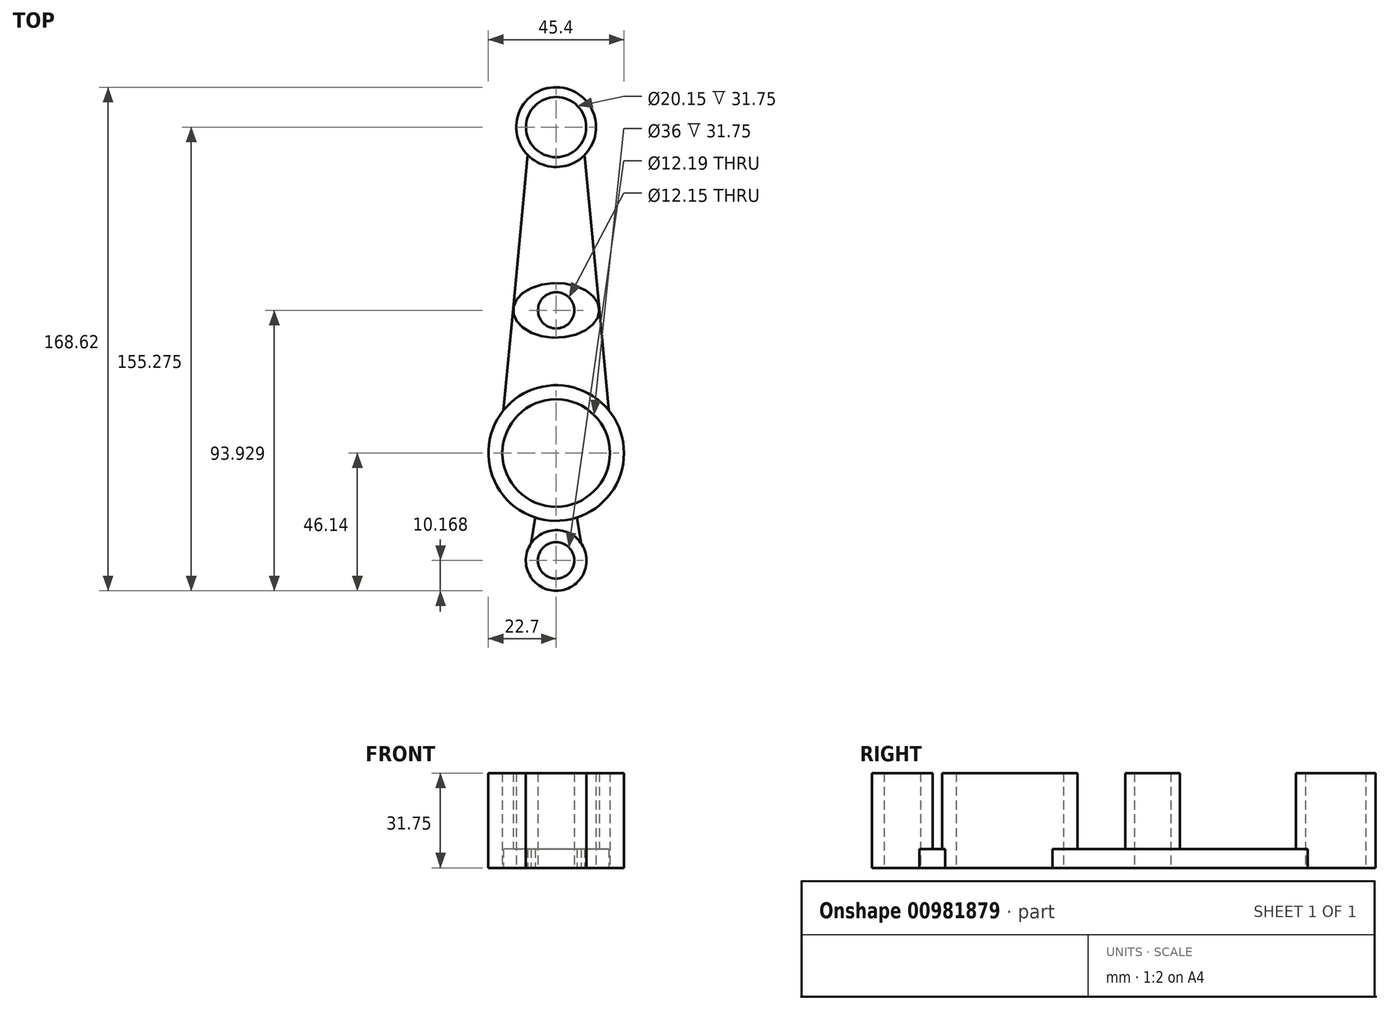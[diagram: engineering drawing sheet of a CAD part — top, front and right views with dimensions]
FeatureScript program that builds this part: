
annotation { "Feature Type Name" : "Feature", "Feature Type Description" : "" }
export const myFeature = defineFeature(function(context is Context, id is Id, definition is map)
    precondition{}
    {
        {
            var Q0;
            Q0=qCreatedBy(makeId("Top.planeOp"),FACE);
            var sketch = newSketch(context, id + "F0", { "sketchPlane" : qUnion([Q0])});
            skCircle(sketch, "E0", {"center": v(0, 0) * mm, "radius": 18 * mm});
            skCircle(sketch, "E1", {"center": v(0, 0) * mm, "radius": 22.7 * mm});
            skCircle(sketch, "E2", {"center": v(0, -35.97) * mm, "radius": 6.1 * mm});
            skCircle(sketch, "E3", {"center": v(0, -35.97) * mm, "radius": 10.16 * mm});
            skCircle(sketch, "E4", {"center": v(0, 47.79) * mm, "radius": 6.07 * mm});
            skCircle(sketch, "E5", {"center": v(0, 109.13) * mm, "radius": 10.08 * mm});
            skCircle(sketch, "E6", {"center": v(0, 109.13) * mm, "radius": 13.35 * mm});
            skEllipse(sketch, "E7", {"center": v(0, 47.79) * mm, "majorRadius": 14.42 * mm, "minorRadius": 9.82 * mm, "majorAxis": v(1, 0)});
            skLineSegment(sketch, "E8", {"start": v(0, 109.13) * mm, "end": v(0, 0) * mm, "construction": true});
            skPoint(sketch, "E9.endSnap0", {"position": v(14.42, 47.79) * mm});
            skLineSegment(sketch, "E10", {"start": v(9.52, 99.78) * mm, "end": v(17.63, 14.3) * mm});
            skLineSegment(sketch, "E11.MirrorCS", {"start": v(-9.52, 99.78) * mm, "end": v(-17.63, 14.3) * mm});
            skLineSegment(sketch, "E12", {"start": v(7.02, -21.58) * mm, "end": v(8.42, -30.27) * mm});
            skLineSegment(sketch, "E13.MirrorCS", {"start": v(-7.02, -21.58) * mm, "end": v(-8.42, -30.27) * mm});
            skSolve(sketch);
        }
        {
            var Q0;
            Q0 = qSketchRegion(id + "F0", true);
            extrude(context, id + "F1", {"entities" : qUnion([Q0]), "depth" : 6.35 * mm, "offsetDistance" : 25.4 * mm});
        }
        {
            var Q0;
            Q0=makeQuery(id+"F1.opExtrude","CAP_FACE",FACE,{"disambiguationData":[OSD([sQuery(id+"F0.wireOp",EDGE,"E0"),sQuery(id+"F0.wireOp",EDGE,"E1"),sQuery(id+"F0.wireOp",EDGE,"E2"),sQuery(id+"F0.wireOp",EDGE,"E3"),sQuery(id+"F0.wireOp",EDGE,"E4"),sQuery(id+"F0.wireOp",EDGE,"E5"),sQuery(id+"F0.wireOp",EDGE,"E6"),sQuery(id+"F0.wireOp",EDGE,"E10"),sQuery(id+"F0.wireOp",EDGE,"E11.MirrorCS"),sQuery(id+"F0.wireOp",EDGE,"E12"),sQuery(id+"F0.wireOp",EDGE,"E13.MirrorCS")])],"isStart":false});
            var sketch = newSketch(context, id + "F2", { "sketchPlane" : qUnion([Q0])});
            skCircle(sketch, "E14", {"center": v(0, 0) * mm, "radius": 18 * mm});
            skCircle(sketch, "E15", {"center": v(0, 0) * mm, "radius": 22.7 * mm});
            skCircle(sketch, "E16", {"center": v(0, -35.97) * mm, "radius": 6.1 * mm});
            skCircle(sketch, "E17", {"center": v(0, -35.97) * mm, "radius": 10.16 * mm});
            skCircle(sketch, "E18", {"center": v(0, 47.79) * mm, "radius": 6.07 * mm});
            skCircle(sketch, "E19", {"center": v(0, 109.13) * mm, "radius": 10.08 * mm});
            skCircle(sketch, "E20", {"center": v(0, 109.13) * mm, "radius": 13.35 * mm});
            skEllipse(sketch, "E21", {"center": v(0, 47.79) * mm, "majorRadius": 14.42 * mm, "minorRadius": 9.15 * mm, "majorAxis": v(1, 0)});
            skLineSegment(sketch, "E22", {"start": v(0, 109.13) * mm, "end": v(0, 0) * mm, "construction": true});
            skPoint(sketch, "E23.endSnap0", {"position": v(14.42, 47.79) * mm});
            skLineSegment(sketch, "E24", {"start": v(9.52, 99.78) * mm, "end": v(17.63, 14.3) * mm});
            skLineSegment(sketch, "E25.MirrorCS", {"start": v(-9.52, 99.78) * mm, "end": v(-17.63, 14.3) * mm});
            skLineSegment(sketch, "E26", {"start": v(7.02, -21.58) * mm, "end": v(8.42, -30.27) * mm});
            skLineSegment(sketch, "E27.MirrorCS", {"start": v(-7.02, -21.58) * mm, "end": v(-8.42, -30.27) * mm});
            skSolve(sketch);
        }
        {
            var Q0;
            Q0=makeQuery(id+"F2.imprint","IMPRINT",FACE,{"disambiguationData":[TD([[makeQuery(id+"F2.imprint","IMPRINT",EDGE,{"derivedFrom":sQuery(id+"F2.wireOp",EDGE,"E16")}),-1.0]])]});
            var Q1;
            Q1=makeQuery(id+"F2.imprint","IMPRINT",FACE,{"disambiguationData":[TD([[makeQuery(id+"F2.imprint","IMPRINT",EDGE,{"derivedFrom":sQuery(id+"F2.wireOp",EDGE,"E19")}),-1.0]])]});
            var Q2;
            Q2=makeQuery(id+"F2.imprint","IMPRINT",FACE,{"disambiguationData":[TD([[makeQuery(id+"F2.imprint","IMPRINT",EDGE,{"derivedFrom":sQuery(id+"F2.wireOp",EDGE,"E14")}),-1.0]])]});
            var Q3;
            Q3=makeQuery(id+"F2.imprint","IMPRINT",FACE,{"disambiguationData":[TD([[makeQuery(id+"F2.imprint","IMPRINT",EDGE,{"derivedFrom":sQuery(id+"F2.wireOp",EDGE,"E18")}),-1.0]])]});
            extrude(context, id + "F3", {"entities" : qUnion([Q0, Q1, Q2, Q3]), "operationType" : NewBodyOperationType.ADD, "depth" : 25.4 * mm, "offsetDistance" : 25.4 * mm});
        }
    });
